# Revit family: EV 220B 65-100 BE
name_source: partatom
category: Pipe Accessories
units: mm (PartAtom-declared; Revit-internal decimal feet)

## family parameters
Always vertical = Yes
Cut with Voids When Loaded = No
Part Type = Valve - Breaks Into
Round Connector Dimension = Use Diameter
Shared = No
Work Plane-Based = No

## types (3) — shared parameters
Body material = Cast iron - Danfoss
IfcExportAs = IfcValveType
IfcExportType = EV220B
LH1 = 20 mm  [stored 0.0656168 ft]
Manufacturer = Danfoss
Max working pressure = 10,0 bar
Medium temperature range = -25 to 90 °C
Mesh size = 300 μm
Seal Material = EPDM
URL = https://www.danfoss.com
W1 = 28 mm  [stored 0.0918635 ft]

## per-type parameters (varying)
| type | B | Connection type | D | DN | Description | Differential pressure | H | H1 | L | Lx | Model | Orifice size | Y | Z | czubek1 | kv-value (m3/h) | walec | wys podst | śr korp | śruby |
| EV220B _DN80_NC_Kvs_75_016D6080 | 130 mm  [stored 0.426509 ft] | Flange 3" EN 1092-1 | 220 mm  [stored 0.721785 ft] | 80 mm | EV220B _DN80_NC_Kvs_75 | 0,25 - 10 bar | 129 mm | 81 mm | 265 mm | 22 mm | 016D6080 | 80,00 mm | 110 mm  [stored 0.360892 ft] | 80 mm | 100 mm  [stored 0.328084 ft] | 75 | 225 mm | 45 mm | 47 mm | 45 mm |
| EV220B _DN65_NC_Kvs_50_016D6065 | 130 mm  [stored 0.426509 ft] | Flange 2 1/2" EN 1092-1 | 185 mm | 65 mm  [stored 0.213255 ft] | EV220B _DN65_NC_Kvs_50 | 0,25 - 10 bar | 129 mm | 85 mm  [stored 0.278871 ft] | 224 mm | 19 mm | 016D6065 | 65,00 mm | 110 mm  [stored 0.360892 ft] | 80 mm | 80 mm | 50 | 190 mm  [stored 0.62336 ft] | 45 mm | 47 mm | 45 mm |
| EV220B _DN100_NC_Kvs_130_016D6100 | 190 mm  [stored 0.62336 ft] | Flange 4" EN 1092-1 | 220 mm  [stored 0.721785 ft] | 100 mm  [stored 0.328084 ft] | EV220B _DN100_NC_Kvs_130 | 0,25 - 10 bar
-25 to 90 °C | 135 mm  [stored 0.442913 ft] | 103 mm  [stored 0.337927 ft] | 315 mm  [stored 1.03346 ft] | 26 mm | 016D6100 | 65,00 mm | 162 mm | 135 mm  [stored 0.442913 ft] | 155 mm  [stored 0.50853 ft] | 130 | 268 mm | 85 mm  [stored 0.278871 ft] | 56 mm  [stored 0.183727 ft] | 70 mm |

note: [stored X ft] marks values corroborated as IEEE doubles in the binary element streams (Revit-internal decimal feet)

## geometry (parser evidence)
native form markers: Sweep x2
no freeform markers — native parametric forms only
